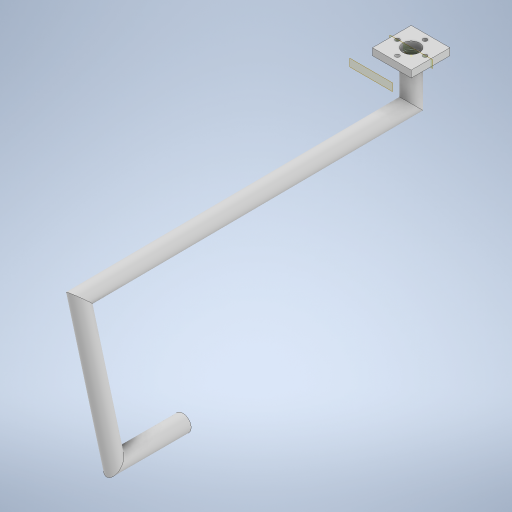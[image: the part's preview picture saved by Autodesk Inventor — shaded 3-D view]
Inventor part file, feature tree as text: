
AUTODESK INVENTOR PART (.ipt)
format: ipt  version: 2023 (Build 270158000, 158)  size: 309,248 bytes
history: native  units: mm
features: sketch x6, extrude x2, plane x2, sweep x1, chamfer x1
ambient origin geometry x8: Origin, YZ Plane, XZ Plane, XY Plane, X Axis, Y Axis, Z Axis, Center Point
bodies: Solid1 (feature_tree)
feature tree (12):
  extrude  "Extrusion1"  Depth=28.0mm
  extrude  "Extrusion2"  Depth=14.0mm
  plane  "Work Plane1"
  sketch  "Sketch3"  dims[d4=5.0mm d5=0.0mm d6=12.0mm]
  sketch  "3D Sketch1"
  sketch  "3D Sketch2"
  sweep  "Sweep1"
  chamfer  "Chamfer1"  Distance=10.0mm
  plane  "Work Plane2"
  sketch  "Sketch1"  dims[d0=28.0mm d1=28.0mm]
  sketch  "Sketch2"  dims[d2=14.0mm d3=14.0mm]
  sketch  "Sketch4"  dims[d7=3.0mm d8=10.0mm d9=40.0mm d11=360.0deg d13=5.0mm d14=0.0mm d15=-14.0mm d16=30.0mm d19=10.0mm d20=0.0mm d21=0.0mm d22=12.0mm d23=1.0mm d24=2.0mm d25=45.0deg d44=15.0mm d53=100.0mm d54=13.962634mm d55=50.0mm d56=240.0mm d57=90.0deg d29=0.0mm d30=0.0mm d31=0.0mm d32=0.0mm]
